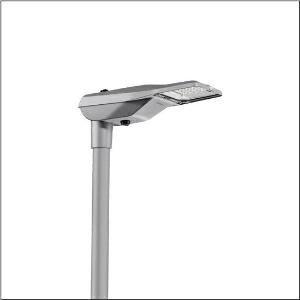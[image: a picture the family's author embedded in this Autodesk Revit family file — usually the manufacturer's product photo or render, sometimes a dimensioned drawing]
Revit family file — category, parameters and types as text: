
# Revit family: streetlight_sl_21_iq_micro___st1_0a_5xe1d61y08cb_da7e
name_source: partatom
category: Lighting Fixtures
units: mm (PartAtom-declared; Revit-internal decimal feet)

## family parameters
Cut with Voids When Loaded = No
Host = Face
Light Source = No
Part Type = Normal
Room Calculation Point = No
Round Connector Dimension = Use Diameter
Shared = No

## types (1)
- --- (1 x LED, 2500 lm, 19.1 W, 2700K)
    Apparent Load = 19 VA
    CIE Flux Codes = 37 72 97 100 100
    Color Rendering = 70
    Color Temperature = 2700K
    Default Elevation = 1800 mm
    Description = Streetlight SL 21 iQ micro, mast luminaire, primary light control with lens, of PMMA, primary optical cover: cover, of toughened safety glass, transparent, light distribution: ST1.0a, light emission: direct distribution, primary light characteristic: asymmetric, installation type: post-top, side-entry, LED, High Power LED, rated luminous flux: 2.500lm, luminous efficacy: 131lm/W, light colour: 727, colour temperature: 2700K, control: presetting dimming logarithmic, Street-Remote, Auto-Match, Temp-Guard, Lumen-Switch, Night-Set, Smart-Wire, Light-Fading, Desk-Remote (wireless, voltage-free reading and setting of iQ features in the workshop via application-optimized NFC function/RFID function), optimised constant luminous flux control (CLO 2.0), mains connection: 220..240V, AC, 50/60Hz, start of lifetime: 19W, end of service life: 20W, reduction: 9W, luminaire housing, of diecast aluminium, powder-coated, Siteco® metallic grey (DB 702S), corrosivity category C5 mid according to DIN EN ISO 12944, please order mast flange separately, inclination adjustable: 0°, 5°, 10°, 15°, sealing non-destructively replaceable, multi-level sealing system, length: 528mm, width: 235mm, height: 110mm, mast flange for spigot size: 42mm (side-entry): 5XC10008XM4, 60/48mm (side-entry/post-top): 5XC10108XM2, 76/60mm (side-entry/post-top): 5XC10108XM1, Smart Interface below and above, protection rating (complete): IP66, insulation class (complete): insulation class II (safety insulation), certification: CE, ENEC, ENEC+, VDE, impact resistance: IK09, permissible operating ambient temperature for outdoor applications: -40..+50°C, standard-compliant lighting for roads and squares, packaging unit: 1 piece

Light Distribution: ST1.0a
    Height = 110 mm
    Lamp = 1 x LED
    Lamp Light Flux = 2500 lm
    Lamp Power = 19.1 W
    Lamp count = 1
    Length = 528 mm
    Luminous efficacy = 131 lm/W
    Manufacturer = Siteco
    ModVariant = No
    Model = 5XE1D61Y08CB
    Number of Poles = 1
    OnlyDefault = Yes
    Power Factor = 1
    Product Name = Streetlight SL 21 iQ micro | ST1.0a
    Product group = mast luminaire | pylon top
    ProductGroupID = 6100
    Protection Class = Protection class II
    Protection Degree = IP 66
    RLX_Detail_Level = 1
    RLX_Emergency_Light_Flux = 0 lm
    RLX_Emergency_Type = 0
    RLX_Emergency_Type_DB = No
    RlxData = <blob elided: 98097 chars, md5=855f5c82>
    Socket = socket
    Standby Power = 0 W
    System Light Flux = 2500 lm
    System Power = 19 W
    Type Comments = factory setting: luminous flux: 100 % | dim-lin: 254 | 387 mA
    Type Image = l_1007239.jpg
    URL = http://relux.com
    VarID = @adj_063729
    Voltage = 0 V
    Weight = 0.00 kg
    Width = 235 mm

## geometry (parser evidence)
native form markers: Blend x4, Sweep x10
no freeform markers — native parametric forms only
